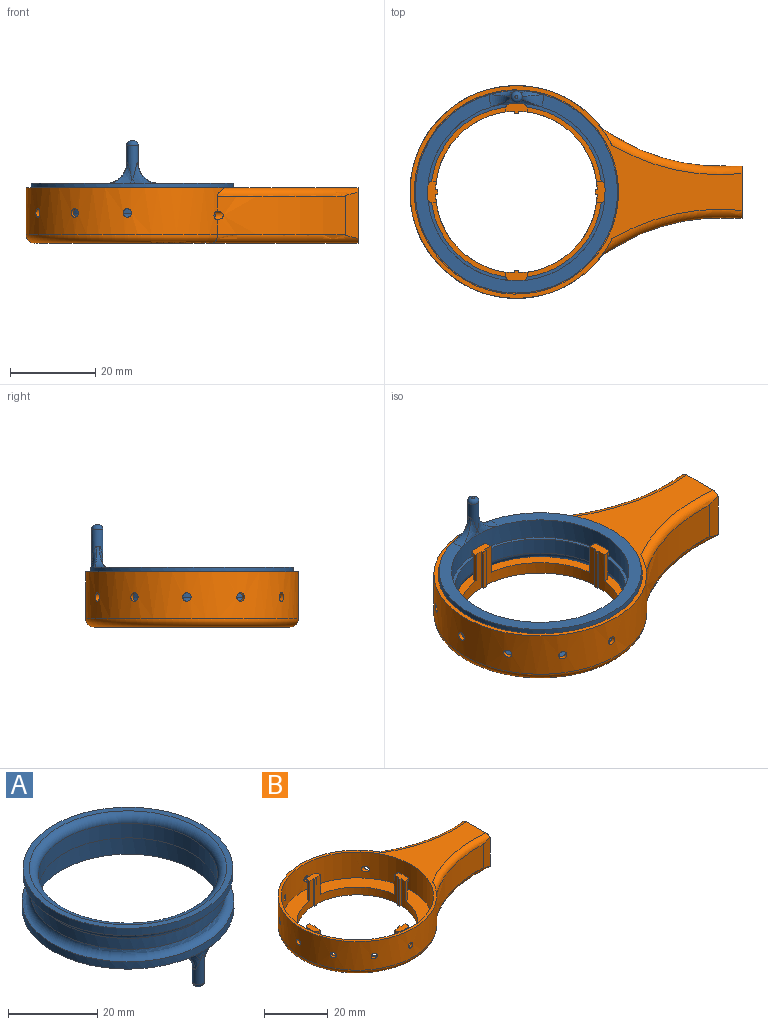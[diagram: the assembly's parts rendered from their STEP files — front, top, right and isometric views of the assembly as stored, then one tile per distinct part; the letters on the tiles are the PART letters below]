
ASSEMBLY  parts=2 mates=1
PART A: 22 faces, bbox 51.4x51.4x21 mm
  f0: bspline ~1.47x1.05mm, area 0.9mm2, adj f1,f4,f10,f18
  f1: bspline ~5.8x5mm, area 9.3mm2, adj f0,f4,f10,f19
  f2: bspline ~5.79x3mm, area 6mm2, adj f3,f9,f10,f21
  f3: bspline ~5.74x5mm, area 9mm2, adj f2,f9,f10,f20
  f4: cylinder r=20.85mm len=41.7mm, axis (0,0,-1), area 655mm2, adj f0,f1,f8,f14,f18
  f5: cylinder r=23.5mm len=47mm, axis (0,0,-1), area 295.3mm2, adj f6,f16
  f6: plane 47x47mm, normal (0,0,1), area 200.6mm2, adj f5,f15
  f7: cylinder r=21.75mm len=43.5mm, axis (0,0,1), area 412.1mm2, adj f16,f17
  f8: plane 47.5x46.64mm, normal (0,0,-1), area 369.7mm2, adj f4,f9,f19,f20
  f9: cylinder r=23.75mm len=47.5mm, axis (0,0,1), area 298.5mm2, adj f2,f3,f8,f17,f21
  f10: cylinder r=1.35mm len=8.14mm, axis (0,0,1), area 46.1mm2, adj f0,f1,f2,f3,f12,f18,f19,f20
  f11: plane 0.7x0.7mm, normal (0,0,-1), area 0.4mm2, adj f12
  f12: torus R=0.35mm, axis (0,0,-1), area 9.7mm2, adj f10,f11
  f13: cylinder r=20.1mm len=40.2mm, axis (0,0,1), area 505.2mm2, adj f14,f15
  f14: plane 41.7x41.7mm, normal (0,0,-1), area 96.5mm2, adj f4,f13
  f15: torus R=22.1mm, axis (0,0,1), area 411.1mm2, adj f6,f13
  f16: torus R=23.75mm, axis (0,0,1), area 406.5mm2, adj f5,f7
  f17: torus R=23.75mm, axis (0,0,-1), area 443.7mm2, adj f7,f9
  f18: bspline ~5.81x5mm, area 9.3mm2, adj f0,f4,f10,f20
  f19: torus R=6.35mm, axis (0,0,-1), area 11.6mm2, adj f1,f8,f10,f21
  f20: torus R=6.35mm, axis (0,0,-1), area 11.6mm2, adj f3,f8,f10,f18
  f21: bspline ~5.74x5mm, area 9mm2, adj f2,f9,f10,f19
PART B: 74 faces, bbox 80.9x54.1x13 mm
  f0: cylinder r=19mm len=18.49mm, axis (0,0,1), area 116.6mm2, adj f10,f13,f16,f17,f37,f38,f62,f71
  f1: cylinder r=19mm len=18.49mm, axis (0,0,1), area 116.6mm2, adj f10,f13,f14,f15,f35,f38,f70,f73
  f2: cylinder r=19mm len=18.49mm, axis (0,0,1), area 116.6mm2, adj f10,f13,f20,f21,f35,f36,f65,f68
  f3: cylinder r=25mm len=50mm, axis (0,0,-1), area 1352.3mm2, adj f9,f11,f22,f29,f31,f32,f33,f34
  f4: cylinder r=24mm len=48mm, axis (0,0,-1), area 1477.6mm2, adj f11,f13,f33,f34,f47,f48,f49,f50
  f5: cylinder r=20mm len=6.5mm, axis (0,0,-1), area 32.6mm2, adj f13,f19,f20,f46
  f6: cylinder r=20mm len=6.5mm, axis (0,0,-1), area 32.6mm2, adj f13,f44,f58,f59
  f7: cylinder r=20mm len=6.5mm, axis (0,0,-1), area 32.6mm2, adj f13,f14,f16,f42
  f8: cylinder r=20mm len=6.5mm, axis (0,0,-1), area 32.6mm2, adj f13,f40,f54,f55
  f9: cylinder r=47.99mm len=30mm, axis (0,0,1), area 284.3mm2, adj f3,f23,f30,f32,f33
  f10: plane 76x46mm, normal (0,0,-1), area 906.1mm2, adj f0,f1,f2,f12,f25,f28,f29,f30
  f11: plane 78x50mm, normal (0,0,1), area 479.2mm2, adj f3,f4,f25,f31,f32
  f12: cylinder r=19mm len=18.49mm, axis (0,0,1), area 116.6mm2, adj f10,f13,f18,f19,f36,f37,f64,f67
  f13: plane 48x48mm, normal (0,0,1), area 655.4mm2, adj f0,f1,f2,f4,f5,f6,f7,f8
  f14: plane 7.5x1.01mm, normal (0,1,0), area 7.6mm2, adj f1,f7,f13,f38,f57
  f15: plane 7.5x0.94mm, normal (1,0,0), area 7mm2, adj f1,f13,f35,f54
  f16: plane 7.5x1.01mm, normal (0,-1,0), area 7.6mm2, adj f0,f7,f13,f38,f56
  f17: plane 7.5x0.99mm, normal (1,0,0), area 7.4mm2, adj f0,f13,f37,f59
  f18: plane 7.5x0.99mm, normal (-1,0,0), area 7.4mm2, adj f12,f13,f37,f58
  f19: plane 7.5x1.01mm, normal (0,-1,0), area 7.6mm2, adj f5,f12,f13,f36,f61
  f20: plane 7.5x1.01mm, normal (0,1,0), area 7.6mm2, adj f2,f5,f13,f36,f60
  f21: plane 7.5x0.94mm, normal (-1,0,0), area 7mm2, adj f2,f13,f35,f55
  f22: cylinder r=47.99mm len=30mm, axis (0,0,1), area 284.3mm2, adj f3,f24,f28,f31,f34
  f23: plane 10.84x3mm, normal (0,-1,0), area 30.4mm2, adj f9,f25,f30,f32
  f24: plane 10.84x3mm, normal (0,1,0), area 30.4mm2, adj f22,f25,f28,f31
  f25: plane 13.03x12.22mm, normal (1,0,0), area 92.6mm2, adj f10,f11,f23,f24,f27,f28,f30,f31
  f26: plane 9x9mm, normal (1,0,0), area 63.6mm2, adj f27
  f27: cylinder r=4.5mm len=26mm, axis (-1,0,0), area 735.1mm2, adj f25,f26
  f28: torus R=49.99mm, axis (0,0,1), area 109.6mm2, adj f10,f22,f24,f25,f29
  f29: torus R=23mm, axis (0,0,1), area 381.7mm2, adj f3,f10,f28,f30
  f30: torus R=49.99mm, axis (0,0,1), area 109.6mm2, adj f9,f10,f23,f25,f29
  f31: torus R=49.99mm, axis (0,0,1), area 103.7mm2, adj f3,f11,f22,f24,f25
  f32: torus R=49.99mm, axis (0,0,1), area 103.7mm2, adj f3,f9,f11,f23,f25
  f33: cylinder r=1mm len=3.53mm, axis (1,0,0), area 9.3mm2, adj f3,f4,f9
  f34: cylinder r=1mm len=3.53mm, axis (1,0,0), area 9.3mm2, adj f3,f4,f22
  f35: plane 5x2.27mm, normal (0,0,1), area 9.2mm2, adj f1,f2,f15,f21,f39,f54,f55,f68
  f36: plane 5x2.34mm, normal (0,0,1), area 9.6mm2, adj f2,f12,f19,f20,f45,f60,f61,f65
  f37: plane 5x2.32mm, normal (0,0,1), area 9.4mm2, adj f0,f12,f17,f18,f43,f58,f59,f62
  f38: plane 5x2.34mm, normal (0,0,1), area 9.6mm2, adj f0,f1,f14,f16,f41,f56,f57,f71
  f39: plane 3x1mm, normal (0,1,0), area 3mm2, adj f35,f40,f54,f55
  f40: plane 4.99x0.93mm, normal (0,0,-1), area 3.7mm2, adj f8,f39,f54,f55
  f41: plane 3x1mm, normal (1,0,0), area 3mm2, adj f38,f42,f56,f57
  f42: plane 5x1mm, normal (0,0,-1), area 4mm2, adj f7,f41,f56,f57
  f43: plane 3x1mm, normal (0,-1,0), area 3mm2, adj f37,f44,f58,f59
  f44: plane 5x0.98mm, normal (0,0,-1), area 3.9mm2, adj f6,f43,f58,f59
  f45: plane 3x1mm, normal (-1,0,0), area 3mm2, adj f36,f46,f60,f61
  f46: plane 5x1mm, normal (0,0,-1), area 4mm2, adj f5,f45,f60,f61
  f47: cylinder r=1mm len=2mm, axis (-1,0,0), area 6.3mm2, adj f3,f4
  f48: cylinder r=1mm len=2mm, axis (0,-1,0), area 6.3mm2, adj f3,f4
  f49: cylinder r=1mm len=2.28mm, axis (-0.5,-0.87,0), area 6.3mm2, adj f3,f4
  f50: cylinder r=1mm len=2.28mm, axis (-0.87,-0.5,0), area 6.3mm2, adj f3,f4
  f51: cylinder r=1mm len=2.28mm, axis (-0.87,0.5,0), area 6.3mm2, adj f3,f4
  f52: cylinder r=1mm len=2.28mm, axis (-0.5,0.87,0), area 6.3mm2, adj f3,f4
  f53: cylinder r=1mm len=2mm, axis (0,1,0), area 6.3mm2, adj f3,f4
  f54: cylinder r=1mm len=7.5mm, axis (0,0,-1), area 2mm2, adj f8,f13,f15,f35,f39,f40
  f55: cylinder r=1mm len=7.5mm, axis (0,0,1), area 2mm2, adj f8,f13,f21,f35,f39,f40
  f56: cylinder r=1mm len=1mm, axis (0,0,1), area 1.6mm2, adj f16,f38,f41,f42
  f57: cylinder r=1mm len=1mm, axis (0,0,-1), area 1.6mm2, adj f14,f38,f41,f42
  f58: cylinder r=1mm len=7.5mm, axis (0,0,1), area 1.7mm2, adj f6,f13,f18,f37,f43,f44
  f59: cylinder r=1mm len=7.5mm, axis (0,0,-1), area 1.7mm2, adj f6,f13,f17,f37,f43,f44
  f60: cylinder r=1mm len=1mm, axis (0,0,1), area 1.6mm2, adj f20,f36,f45,f46
  f61: cylinder r=1mm len=1mm, axis (0,0,-1), area 1.6mm2, adj f19,f36,f45,f46
  f62: plane 10.5x0.49mm, normal (1,0,0), area 5.2mm2, adj f0,f10,f37,f63
  f63: plane 10.5x1mm, normal (0,1,0), area 10.5mm2, adj f10,f37,f62,f64
  f64: plane 10.5x0.49mm, normal (-1,0,0), area 5.2mm2, adj f10,f12,f37,f63
  f65: plane 10.5x0.49mm, normal (0,1,0), area 5.1mm2, adj f2,f10,f36,f66
  f66: plane 10.5x1mm, normal (1,0,0), area 10.5mm2, adj f10,f36,f65,f67
  f67: plane 10.5x0.49mm, normal (0,-1,0), area 5.1mm2, adj f10,f12,f36,f66
  f68: plane 10.5x0.49mm, normal (-1,0,0), area 5.2mm2, adj f2,f10,f35,f69
  f69: plane 10.5x1mm, normal (0,-1,0), area 10.5mm2, adj f10,f35,f68,f70
  f70: plane 10.5x0.49mm, normal (1,0,0), area 5.2mm2, adj f1,f10,f35,f69
  f71: plane 10.5x0.49mm, normal (0,-1,0), area 5.2mm2, adj f0,f10,f38,f72
  f72: plane 10.5x1mm, normal (-1,0,0), area 10.5mm2, adj f10,f38,f71,f73
  f73: plane 10.5x0.49mm, normal (0,1,0), area 5.2mm2, adj f1,f10,f38,f72
PLACE A rot(axis=(1,0,0),180deg) t=(10.16,-62.89,2.7)mm
PLACE B t=(10.16,-62.89,-2.3)mm
MATE revolute A.f5 <-> B.f5  axis (0,0,-1) through (10.16,-62.89,0.7)mm
